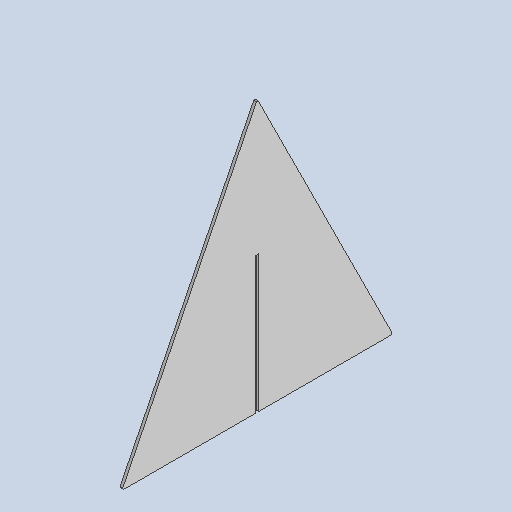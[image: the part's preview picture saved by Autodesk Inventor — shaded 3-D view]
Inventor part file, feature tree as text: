
AUTODESK INVENTOR PART (.ipt)
format: ipt  version: 2025 (Build 290162010, 162A)  size: 281,600 bytes
history: native  units: mm
features: other x5, sketch x2, sheet_metal_op x1, extrude x1
ambient origin geometry x8: Origin, YZ Plane, XZ Plane, XY Plane, X Axis, Y Axis, Z Axis, Center Point
bodies: Solid1 (feature_tree)
feature tree (9):
  other  "MSC 207 CONE BLADE"
  sheet_metal_op  "Face1"
  extrude  "Extrusion2"  Depth=300.0mm
  other  "Corner Chamfer1"
  other  "Corner Chamfer2"
  sketch  "Sketch1"  dims[d0=300.0mm d1=300.0mm]
  other  "Plate1"
  sketch  "Sketch3"  dims[d2=3.0mm d7=3.2mm d8=151.0mm d9=0.0mm d10=0.0mm d11=2.0mm d12=6.0mm d13=45.0deg d14=2.0mm d15=6.0mm d16=45.0deg]
  other  "Definition1"
